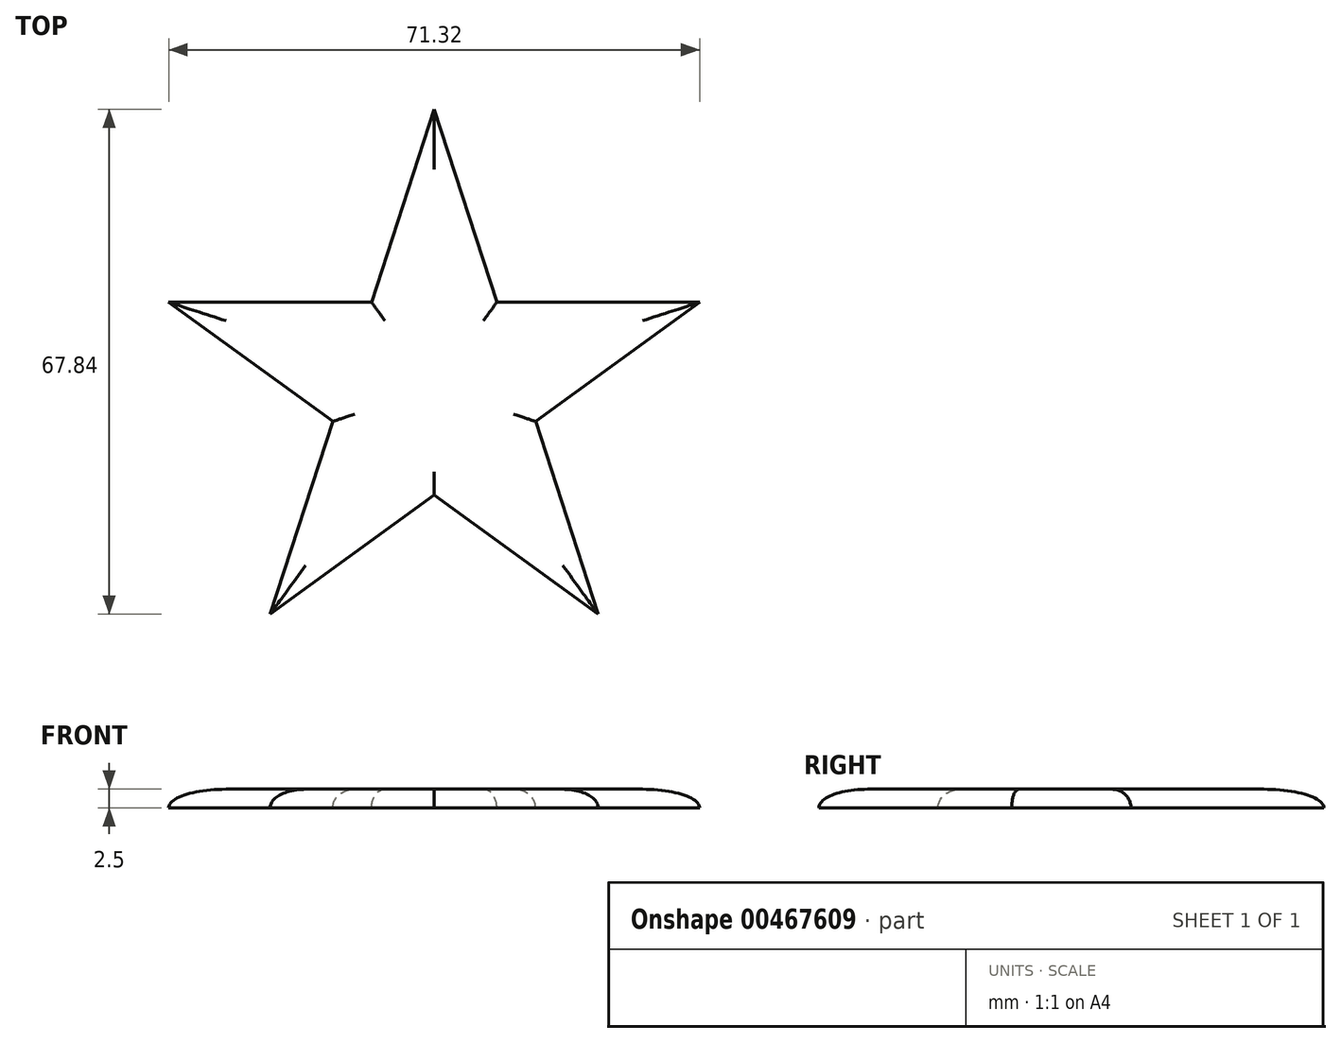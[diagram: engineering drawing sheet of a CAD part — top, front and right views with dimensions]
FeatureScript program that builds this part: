
annotation { "Feature Type Name" : "Feature", "Feature Type Description" : "" }
export const myFeature = defineFeature(function(context is Context, id is Id, definition is map)
    precondition{}
    {
        {
            var Q0;
            Q0=qCreatedBy(makeId("Top.planeOp"),FACE);
            var sketch = newSketch(context, id + "F0", { "sketchPlane" : qUnion([Q0])});
            skCircle(sketch, "E0", {"center": v(0, 0) * mm, "radius": 37.5 * mm, "construction": true});
            skLineSegment(sketch, "E1", {"start": v(0, 0) * mm, "end": v(0, 37.5) * mm, "construction": true});
            skLineSegment(sketch, "E2", {"start": v(0, 0) * mm, "end": v(35.66, 11.59) * mm, "construction": true});
            skLineSegment(sketch, "E3", {"start": v(0, 0) * mm, "end": v(22.04, -30.34) * mm, "construction": true});
            skLineSegment(sketch, "E4", {"start": v(0, 0) * mm, "end": v(-22.04, -30.34) * mm, "construction": true});
            skLineSegment(sketch, "E5", {"start": v(0, 0) * mm, "end": v(-35.66, 11.59) * mm, "construction": true});
            skLineSegment(sketch, "E6", {"start": v(-35.66, 11.59) * mm, "end": v(-8.42, 11.59) * mm});
            skLineSegment(sketch, "E7", {"start": v(22.04, -30.34) * mm, "end": v(13.62, -4.43) * mm});
            skLineSegment(sketch, "E8", {"start": v(-13.62, -4.43) * mm, "end": v(-22.04, -30.34) * mm});
            skLineSegment(sketch, "E9", {"start": v(0, -14.32) * mm, "end": v(22.04, -30.34) * mm});
            skLineSegment(sketch, "E10", {"start": v(8.42, 11.59) * mm, "end": v(35.66, 11.59) * mm});
            skLineSegment(sketch, "E11", {"start": v(-35.66, 11.59) * mm, "end": v(-13.62, -4.43) * mm});
            skLineSegment(sketch, "E12", {"start": v(-8.42, 11.59) * mm, "end": v(0, 37.5) * mm});
            skLineSegment(sketch, "E13", {"start": v(-22.04, -30.34) * mm, "end": v(0, -14.32) * mm});
            skLineSegment(sketch, "E14", {"start": v(13.62, -4.43) * mm, "end": v(35.66, 11.59) * mm});
            skLineSegment(sketch, "E15", {"start": v(0, 37.5) * mm, "end": v(8.42, 11.59) * mm});
            skSolve(sketch);
        }
        {
            var Q0;
            Q0=makeQuery(id+"F0.imprint","IMPRINT",FACE,{"disambiguationData":[TD([[makeQuery(id+"F0.imprint","IMPRINT",EDGE,{"derivedFrom":sQuery(id+"F0.wireOp",EDGE,"E6")}),-1.0]])]});
            extrude(context, id + "F1", {"entities" : qUnion([Q0]), "depth" : 2.5 * mm});
        }
        {
            var Q0;
            Q0=makeQuery(id+"F1.opExtrude","CAP_EDGE",EDGE,{"disambiguationData":[OSD([sQuery(id+"F0.wireOp",EDGE,"E12")])],"isStart":false});
            var Q1;
            Q1=makeQuery(id+"F1.opExtrude","CAP_EDGE",EDGE,{"disambiguationData":[OSD([sQuery(id+"F0.wireOp",EDGE,"E6")])],"isStart":false});
            var Q2;
            Q2=makeQuery(id+"F1.opExtrude","CAP_EDGE",EDGE,{"disambiguationData":[OSD([sQuery(id+"F0.wireOp",EDGE,"E11")])],"isStart":false});
            var Q3;
            Q3=makeQuery(id+"F1.opExtrude","CAP_EDGE",EDGE,{"disambiguationData":[OSD([sQuery(id+"F0.wireOp",EDGE,"E8")])],"isStart":false});
            var Q4;
            Q4=makeQuery(id+"F1.opExtrude","CAP_EDGE",EDGE,{"disambiguationData":[OSD([sQuery(id+"F0.wireOp",EDGE,"E9")])],"isStart":false});
            var Q5;
            Q5=makeQuery(id+"F1.opExtrude","CAP_EDGE",EDGE,{"disambiguationData":[OSD([sQuery(id+"F0.wireOp",EDGE,"E7")])],"isStart":false});
            var Q6;
            Q6=makeQuery(id+"F1.opExtrude","CAP_EDGE",EDGE,{"disambiguationData":[OSD([sQuery(id+"F0.wireOp",EDGE,"E14")])],"isStart":false});
            var Q7;
            Q7=makeQuery(id+"F1.opExtrude","CAP_EDGE",EDGE,{"disambiguationData":[OSD([sQuery(id+"F0.wireOp",EDGE,"E10")])],"isStart":false});
            var Q8;
            Q8=makeQuery(id+"F1.opExtrude","CAP_EDGE",EDGE,{"disambiguationData":[OSD([sQuery(id+"F0.wireOp",EDGE,"E15")])],"isStart":false});
            var Q9;
            Q9=makeQuery(id+"F1.opExtrude","CAP_FACE",FACE,{"disambiguationData":[OSD([sQuery(id+"F0.wireOp",EDGE,"E6"),sQuery(id+"F0.wireOp",EDGE,"E7"),sQuery(id+"F0.wireOp",EDGE,"E8"),sQuery(id+"F0.wireOp",EDGE,"E9"),sQuery(id+"F0.wireOp",EDGE,"E10"),sQuery(id+"F0.wireOp",EDGE,"E11"),sQuery(id+"F0.wireOp",EDGE,"E12"),sQuery(id+"F0.wireOp",EDGE,"E13"),sQuery(id+"F0.wireOp",EDGE,"E14"),sQuery(id+"F0.wireOp",EDGE,"E15")])],"isStart":false});
            fillet(context, id + "F2", {"entities" : qUnion([Q0, Q1, Q2, Q3, Q4, Q5, Q6, Q7, Q8, Q9]), "radius" : 2.5 * mm, "tangentPropagation" : true, "allowEdgeOverflow" : false});
        }
    });
